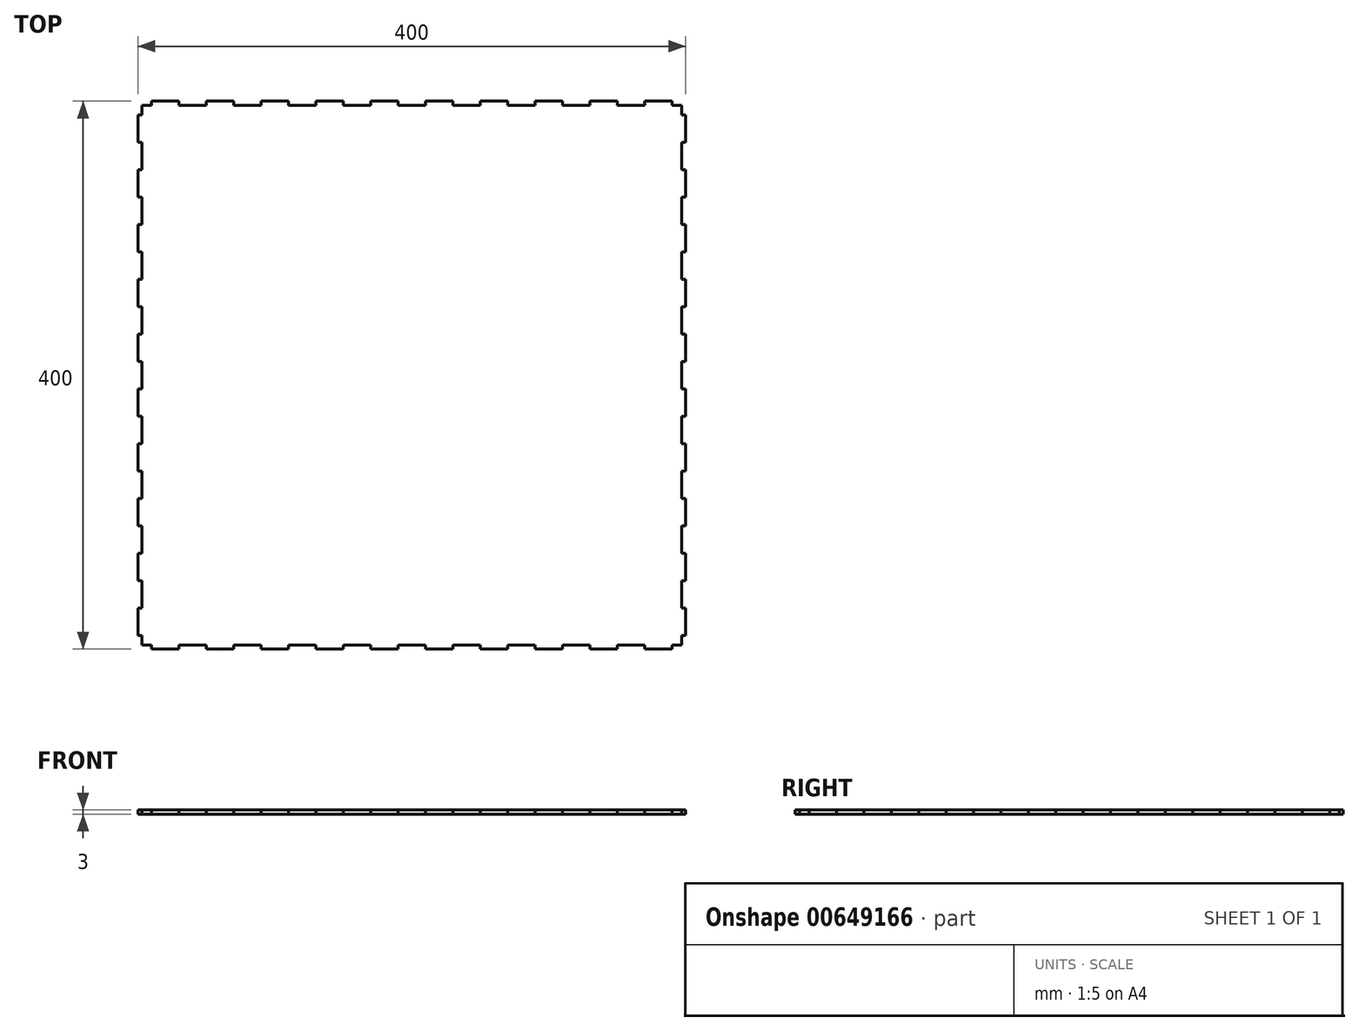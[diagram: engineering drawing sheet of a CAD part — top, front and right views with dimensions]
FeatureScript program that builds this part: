
annotation { "Feature Type Name" : "Feature", "Feature Type Description" : "" }
export const myFeature = defineFeature(function(context is Context, id is Id, definition is map)
    precondition{}
    {
        {
            var Q0;
            Q0=qCreatedBy(makeId("Top.planeOp"),FACE);
            var sketch = newSketch(context, id + "F0", { "sketchPlane" : qUnion([Q0])});
            skLineSegment(sketch, "E0.bottom", {"start": v(197, 197) * mm, "end": v(-197, 197) * mm});
            skLineSegment(sketch, "E0.top", {"start": v(197, -197) * mm, "end": v(-197, -197) * mm});
            skLineSegment(sketch, "E0.left", {"start": v(197, 197) * mm, "end": v(197, -197) * mm});
            skLineSegment(sketch, "E0.right", {"start": v(-197, 197) * mm, "end": v(-197, -197) * mm});
            skPoint(sketch, "E0.middle", {"position": v(0, 0) * mm});
            skSolve(sketch);
        }
        {
            var Q0;
            Q0 = qSketchRegion(id + "F0", true);
            extrude(context, id + "F1", {"entities" : qUnion([Q0]), "depth" : 3 * mm, "offsetDistance" : 25 * mm});
        }
        {
            var Q0;
            Q0=makeQuery(id+"F1.opExtrude","CAP_FACE",FACE,{"disambiguationData":[OSD([sQuery(id+"F0.wireOp",EDGE,"E0.bottom"),sQuery(id+"F0.wireOp",EDGE,"E0.top"),sQuery(id+"F0.wireOp",EDGE,"E0.left"),sQuery(id+"F0.wireOp",EDGE,"E0.right")])],"isStart":false});
            var sketch = newSketch(context, id + "F2", { "sketchPlane" : qUnion([Q0])});
            skLineSegment(sketch, "E1", {"start": v(-197, -197) * mm, "end": v(-190, -197) * mm, "construction": true});
            skLineSegment(sketch, "E2.bottom", {"start": v(-190, -197) * mm, "end": v(-170, -197) * mm});
            skLineSegment(sketch, "E2.top", {"start": v(-190, -200) * mm, "end": v(-170, -200) * mm});
            skLineSegment(sketch, "E2.left", {"start": v(-190, -197) * mm, "end": v(-190, -200) * mm});
            skLineSegment(sketch, "E2.right", {"start": v(-170, -197) * mm, "end": v(-170, -200) * mm});
            skLineSegment(sketch, "E3.1.0.0", {"start": v(-150, -197) * mm, "end": v(-130, -197) * mm});
            skLineSegment(sketch, "E3.1.0.1", {"start": v(-150, -197) * mm, "end": v(-150, -200) * mm});
            skLineSegment(sketch, "E3.1.0.2", {"start": v(-150, -200) * mm, "end": v(-130, -200) * mm});
            skLineSegment(sketch, "E3.1.0.3", {"start": v(-130, -197) * mm, "end": v(-130, -200) * mm});
            skLineSegment(sketch, "E3.2.0.0", {"start": v(-110, -197) * mm, "end": v(-90, -197) * mm});
            skLineSegment(sketch, "E3.2.0.1", {"start": v(-110, -197) * mm, "end": v(-110, -200) * mm});
            skLineSegment(sketch, "E3.2.0.2", {"start": v(-110, -200) * mm, "end": v(-90, -200) * mm});
            skLineSegment(sketch, "E3.2.0.3", {"start": v(-90, -197) * mm, "end": v(-90, -200) * mm});
            skLineSegment(sketch, "E3.direction1", {"start": v(-190, -197) * mm, "end": v(-150, -197) * mm, "construction": true});
            skLineSegment(sketch, "E4.0.3.0", {"start": v(-70, -197) * mm, "end": v(-50, -197) * mm});
            skLineSegment(sketch, "E4.3.3.0", {"start": v(-70, -197) * mm, "end": v(-70, -200) * mm});
            skLineSegment(sketch, "E4.6.3.0", {"start": v(-70, -200) * mm, "end": v(-50, -200) * mm});
            skLineSegment(sketch, "E4.9.3.0", {"start": v(-50, -197) * mm, "end": v(-50, -200) * mm});
            skLineSegment(sketch, "E4.0.4.0", {"start": v(-30, -197) * mm, "end": v(-10, -197) * mm});
            skLineSegment(sketch, "E4.3.4.0", {"start": v(-30, -197) * mm, "end": v(-30, -200) * mm});
            skLineSegment(sketch, "E4.6.4.0", {"start": v(-30, -200) * mm, "end": v(-10, -200) * mm});
            skLineSegment(sketch, "E4.9.4.0", {"start": v(-10, -197) * mm, "end": v(-10, -200) * mm});
            skLineSegment(sketch, "E4.0.5.0", {"start": v(10, -197) * mm, "end": v(30, -197) * mm});
            skLineSegment(sketch, "E4.3.5.0", {"start": v(10, -197) * mm, "end": v(10, -200) * mm});
            skLineSegment(sketch, "E4.6.5.0", {"start": v(10, -200) * mm, "end": v(30, -200) * mm});
            skLineSegment(sketch, "E4.9.5.0", {"start": v(30, -197) * mm, "end": v(30, -200) * mm});
            skLineSegment(sketch, "E4.0.6.0", {"start": v(50, -197) * mm, "end": v(70, -197) * mm});
            skLineSegment(sketch, "E4.3.6.0", {"start": v(50, -197) * mm, "end": v(50, -200) * mm});
            skLineSegment(sketch, "E4.6.6.0", {"start": v(50, -200) * mm, "end": v(70, -200) * mm});
            skLineSegment(sketch, "E4.9.6.0", {"start": v(70, -197) * mm, "end": v(70, -200) * mm});
            skLineSegment(sketch, "E4.0.7.0", {"start": v(90, -197) * mm, "end": v(110, -197) * mm});
            skLineSegment(sketch, "E4.3.7.0", {"start": v(90, -197) * mm, "end": v(90, -200) * mm});
            skLineSegment(sketch, "E4.6.7.0", {"start": v(90, -200) * mm, "end": v(110, -200) * mm});
            skLineSegment(sketch, "E4.9.7.0", {"start": v(110, -197) * mm, "end": v(110, -200) * mm});
            skLineSegment(sketch, "E4.0.8.0", {"start": v(130, -197) * mm, "end": v(150, -197) * mm});
            skLineSegment(sketch, "E4.3.8.0", {"start": v(130, -197) * mm, "end": v(130, -200) * mm});
            skLineSegment(sketch, "E4.6.8.0", {"start": v(130, -200) * mm, "end": v(150, -200) * mm});
            skLineSegment(sketch, "E4.9.8.0", {"start": v(150, -197) * mm, "end": v(150, -200) * mm});
            skLineSegment(sketch, "E5.0.9.0", {"start": v(170, -197) * mm, "end": v(190, -197) * mm});
            skLineSegment(sketch, "E5.3.9.0", {"start": v(170, -197) * mm, "end": v(170, -200) * mm});
            skLineSegment(sketch, "E5.6.9.0", {"start": v(170, -200) * mm, "end": v(190, -200) * mm});
            skLineSegment(sketch, "E5.9.9.0", {"start": v(190, -197) * mm, "end": v(190, -200) * mm});
            skLineSegment(sketch, "E6.1.0", {"start": v(197, 10) * mm, "end": v(197, 30) * mm});
            skLineSegment(sketch, "E6.1.1", {"start": v(197, 170) * mm, "end": v(197, 190) * mm});
            skLineSegment(sketch, "E6.1.2", {"start": v(200, -110) * mm, "end": v(200, -90) * mm});
            skLineSegment(sketch, "E6.1.3", {"start": v(197, -110) * mm, "end": v(197, -90) * mm});
            skLineSegment(sketch, "E6.1.4", {"start": v(200, -150) * mm, "end": v(200, -130) * mm});
            skLineSegment(sketch, "E6.1.5", {"start": v(197, 50) * mm, "end": v(197, 70) * mm});
            skLineSegment(sketch, "E6.1.6", {"start": v(197, -30) * mm, "end": v(197, -10) * mm});
            skLineSegment(sketch, "E6.1.7", {"start": v(197, 130) * mm, "end": v(197, 150) * mm});
            skLineSegment(sketch, "E6.1.8", {"start": v(197, -150) * mm, "end": v(197, -130) * mm});
            skLineSegment(sketch, "E6.1.9", {"start": v(197, -70) * mm, "end": v(197, -50) * mm});
            skLineSegment(sketch, "E6.1.10", {"start": v(197, -190) * mm, "end": v(197, -150) * mm, "construction": true});
            skLineSegment(sketch, "E6.1.11", {"start": v(197, 90) * mm, "end": v(197, 110) * mm});
            skLineSegment(sketch, "E6.1.12", {"start": v(200, 10) * mm, "end": v(200, 30) * mm});
            skLineSegment(sketch, "E6.1.13", {"start": v(200, 170) * mm, "end": v(200, 190) * mm});
            skLineSegment(sketch, "E6.1.14", {"start": v(200, 50) * mm, "end": v(200, 70) * mm});
            skLineSegment(sketch, "E6.1.15", {"start": v(200, -70) * mm, "end": v(200, -50) * mm});
            skLineSegment(sketch, "E6.1.16", {"start": v(200, 90) * mm, "end": v(200, 110) * mm});
            skLineSegment(sketch, "E6.1.17", {"start": v(200, -30) * mm, "end": v(200, -10) * mm});
            skLineSegment(sketch, "E6.1.18", {"start": v(200, 130) * mm, "end": v(200, 150) * mm});
            skLineSegment(sketch, "E6.1.19", {"start": v(200, -190) * mm, "end": v(200, -170) * mm});
            skLineSegment(sketch, "E6.1.20", {"start": v(197, -190) * mm, "end": v(197, -170) * mm});
            skLineSegment(sketch, "E6.1.21", {"start": v(197, -90) * mm, "end": v(200, -90) * mm});
            skLineSegment(sketch, "E6.1.22", {"start": v(197, 30) * mm, "end": v(200, 30) * mm});
            skLineSegment(sketch, "E6.1.23", {"start": v(197, 190) * mm, "end": v(200, 190) * mm});
            skLineSegment(sketch, "E6.1.24", {"start": v(197, -110) * mm, "end": v(200, -110) * mm});
            skLineSegment(sketch, "E6.1.25", {"start": v(197, 130) * mm, "end": v(200, 130) * mm});
            skLineSegment(sketch, "E6.1.26", {"start": v(197, -30) * mm, "end": v(200, -30) * mm});
            skLineSegment(sketch, "E6.1.27", {"start": v(197, 170) * mm, "end": v(200, 170) * mm});
            skLineSegment(sketch, "E6.1.28", {"start": v(197, 90) * mm, "end": v(200, 90) * mm});
            skLineSegment(sketch, "E6.1.29", {"start": v(197, -170) * mm, "end": v(200, -170) * mm});
            skLineSegment(sketch, "E6.1.30", {"start": v(197, -70) * mm, "end": v(200, -70) * mm});
            skLineSegment(sketch, "E6.1.31", {"start": v(197, -50) * mm, "end": v(200, -50) * mm});
            skLineSegment(sketch, "E6.1.32", {"start": v(197, 110) * mm, "end": v(200, 110) * mm});
            skLineSegment(sketch, "E6.1.33", {"start": v(197, -10) * mm, "end": v(200, -10) * mm});
            skLineSegment(sketch, "E6.1.34", {"start": v(197, 150) * mm, "end": v(200, 150) * mm});
            skLineSegment(sketch, "E6.1.35", {"start": v(197, 50) * mm, "end": v(200, 50) * mm});
            skLineSegment(sketch, "E6.1.36", {"start": v(197, 70) * mm, "end": v(200, 70) * mm});
            skLineSegment(sketch, "E6.1.37", {"start": v(197, 10) * mm, "end": v(200, 10) * mm});
            skLineSegment(sketch, "E6.1.38", {"start": v(197, -130) * mm, "end": v(200, -130) * mm});
            skLineSegment(sketch, "E6.1.39", {"start": v(197, -150) * mm, "end": v(200, -150) * mm});
            skLineSegment(sketch, "E6.1.40", {"start": v(197, -190) * mm, "end": v(200, -190) * mm});
            skLineSegment(sketch, "E6.1.41", {"start": v(197, -197) * mm, "end": v(197, -190) * mm, "construction": true});
            skLineSegment(sketch, "E6.2.0", {"start": v(-10, 197) * mm, "end": v(-30, 197) * mm});
            skLineSegment(sketch, "E6.2.1", {"start": v(-170, 197) * mm, "end": v(-190, 197) * mm});
            skLineSegment(sketch, "E6.2.2", {"start": v(110, 200) * mm, "end": v(90, 200) * mm});
            skLineSegment(sketch, "E6.2.3", {"start": v(110, 197) * mm, "end": v(90, 197) * mm});
            skLineSegment(sketch, "E6.2.4", {"start": v(150, 200) * mm, "end": v(130, 200) * mm});
            skLineSegment(sketch, "E6.2.5", {"start": v(-50, 197) * mm, "end": v(-70, 197) * mm});
            skLineSegment(sketch, "E6.2.6", {"start": v(30, 197) * mm, "end": v(10, 197) * mm});
            skLineSegment(sketch, "E6.2.7", {"start": v(-130, 197) * mm, "end": v(-150, 197) * mm});
            skLineSegment(sketch, "E6.2.8", {"start": v(150, 197) * mm, "end": v(130, 197) * mm});
            skLineSegment(sketch, "E6.2.9", {"start": v(70, 197) * mm, "end": v(50, 197) * mm});
            skLineSegment(sketch, "E6.2.10", {"start": v(190, 197) * mm, "end": v(150, 197) * mm, "construction": true});
            skLineSegment(sketch, "E6.2.11", {"start": v(-90, 197) * mm, "end": v(-110, 197) * mm});
            skLineSegment(sketch, "E6.2.12", {"start": v(-10, 200) * mm, "end": v(-30, 200) * mm});
            skLineSegment(sketch, "E6.2.13", {"start": v(-170, 200) * mm, "end": v(-190, 200) * mm});
            skLineSegment(sketch, "E6.2.14", {"start": v(-50, 200) * mm, "end": v(-70, 200) * mm});
            skLineSegment(sketch, "E6.2.15", {"start": v(70, 200) * mm, "end": v(50, 200) * mm});
            skLineSegment(sketch, "E6.2.16", {"start": v(-90, 200) * mm, "end": v(-110, 200) * mm});
            skLineSegment(sketch, "E6.2.17", {"start": v(30, 200) * mm, "end": v(10, 200) * mm});
            skLineSegment(sketch, "E6.2.18", {"start": v(-130, 200) * mm, "end": v(-150, 200) * mm});
            skLineSegment(sketch, "E6.2.19", {"start": v(190, 200) * mm, "end": v(170, 200) * mm});
            skLineSegment(sketch, "E6.2.20", {"start": v(190, 197) * mm, "end": v(170, 197) * mm});
            skLineSegment(sketch, "E6.2.21", {"start": v(90, 197) * mm, "end": v(90, 200) * mm});
            skLineSegment(sketch, "E6.2.22", {"start": v(-30, 197) * mm, "end": v(-30, 200) * mm});
            skLineSegment(sketch, "E6.2.23", {"start": v(-190, 197) * mm, "end": v(-190, 200) * mm});
            skLineSegment(sketch, "E6.2.24", {"start": v(110, 197) * mm, "end": v(110, 200) * mm});
            skLineSegment(sketch, "E6.2.25", {"start": v(-130, 197) * mm, "end": v(-130, 200) * mm});
            skLineSegment(sketch, "E6.2.26", {"start": v(30, 197) * mm, "end": v(30, 200) * mm});
            skLineSegment(sketch, "E6.2.27", {"start": v(-170, 197) * mm, "end": v(-170, 200) * mm});
            skLineSegment(sketch, "E6.2.28", {"start": v(-90, 197) * mm, "end": v(-90, 200) * mm});
            skLineSegment(sketch, "E6.2.29", {"start": v(170, 197) * mm, "end": v(170, 200) * mm});
            skLineSegment(sketch, "E6.2.30", {"start": v(70, 197) * mm, "end": v(70, 200) * mm});
            skLineSegment(sketch, "E6.2.31", {"start": v(50, 197) * mm, "end": v(50, 200) * mm});
            skLineSegment(sketch, "E6.2.32", {"start": v(-110, 197) * mm, "end": v(-110, 200) * mm});
            skLineSegment(sketch, "E6.2.33", {"start": v(10, 197) * mm, "end": v(10, 200) * mm});
            skLineSegment(sketch, "E6.2.34", {"start": v(-150, 197) * mm, "end": v(-150, 200) * mm});
            skLineSegment(sketch, "E6.2.35", {"start": v(-50, 197) * mm, "end": v(-50, 200) * mm});
            skLineSegment(sketch, "E6.2.36", {"start": v(-70, 197) * mm, "end": v(-70, 200) * mm});
            skLineSegment(sketch, "E6.2.37", {"start": v(-10, 197) * mm, "end": v(-10, 200) * mm});
            skLineSegment(sketch, "E6.2.38", {"start": v(130, 197) * mm, "end": v(130, 200) * mm});
            skLineSegment(sketch, "E6.2.39", {"start": v(150, 197) * mm, "end": v(150, 200) * mm});
            skLineSegment(sketch, "E6.2.40", {"start": v(190, 197) * mm, "end": v(190, 200) * mm});
            skLineSegment(sketch, "E6.2.41", {"start": v(197, 197) * mm, "end": v(190, 197) * mm, "construction": true});
            skLineSegment(sketch, "E6.3.0", {"start": v(-197, -10) * mm, "end": v(-197, -30) * mm});
            skLineSegment(sketch, "E6.3.1", {"start": v(-197, -170) * mm, "end": v(-197, -190) * mm});
            skLineSegment(sketch, "E6.3.2", {"start": v(-200, 110) * mm, "end": v(-200, 90) * mm});
            skLineSegment(sketch, "E6.3.3", {"start": v(-197, 110) * mm, "end": v(-197, 90) * mm});
            skLineSegment(sketch, "E6.3.4", {"start": v(-200, 150) * mm, "end": v(-200, 130) * mm});
            skLineSegment(sketch, "E6.3.5", {"start": v(-197, -50) * mm, "end": v(-197, -70) * mm});
            skLineSegment(sketch, "E6.3.6", {"start": v(-197, 30) * mm, "end": v(-197, 10) * mm});
            skLineSegment(sketch, "E6.3.7", {"start": v(-197, -130) * mm, "end": v(-197, -150) * mm});
            skLineSegment(sketch, "E6.3.8", {"start": v(-197, 150) * mm, "end": v(-197, 130) * mm});
            skLineSegment(sketch, "E6.3.9", {"start": v(-197, 70) * mm, "end": v(-197, 50) * mm});
            skLineSegment(sketch, "E6.3.10", {"start": v(-197, 190) * mm, "end": v(-197, 150) * mm, "construction": true});
            skLineSegment(sketch, "E6.3.11", {"start": v(-197, -90) * mm, "end": v(-197, -110) * mm});
            skLineSegment(sketch, "E6.3.12", {"start": v(-200, -10) * mm, "end": v(-200, -30) * mm});
            skLineSegment(sketch, "E6.3.13", {"start": v(-200, -170) * mm, "end": v(-200, -190) * mm});
            skLineSegment(sketch, "E6.3.14", {"start": v(-200, -50) * mm, "end": v(-200, -70) * mm});
            skLineSegment(sketch, "E6.3.15", {"start": v(-200, 70) * mm, "end": v(-200, 50) * mm});
            skLineSegment(sketch, "E6.3.16", {"start": v(-200, -90) * mm, "end": v(-200, -110) * mm});
            skLineSegment(sketch, "E6.3.17", {"start": v(-200, 30) * mm, "end": v(-200, 10) * mm});
            skLineSegment(sketch, "E6.3.18", {"start": v(-200, -130) * mm, "end": v(-200, -150) * mm});
            skLineSegment(sketch, "E6.3.19", {"start": v(-200, 190) * mm, "end": v(-200, 170) * mm});
            skLineSegment(sketch, "E6.3.20", {"start": v(-197, 190) * mm, "end": v(-197, 170) * mm});
            skLineSegment(sketch, "E6.3.21", {"start": v(-197, 90) * mm, "end": v(-200, 90) * mm});
            skLineSegment(sketch, "E6.3.22", {"start": v(-197, -30) * mm, "end": v(-200, -30) * mm});
            skLineSegment(sketch, "E6.3.23", {"start": v(-197, -190) * mm, "end": v(-200, -190) * mm});
            skLineSegment(sketch, "E6.3.24", {"start": v(-197, 110) * mm, "end": v(-200, 110) * mm});
            skLineSegment(sketch, "E6.3.25", {"start": v(-197, -130) * mm, "end": v(-200, -130) * mm});
            skLineSegment(sketch, "E6.3.26", {"start": v(-197, 30) * mm, "end": v(-200, 30) * mm});
            skLineSegment(sketch, "E6.3.27", {"start": v(-197, -170) * mm, "end": v(-200, -170) * mm});
            skLineSegment(sketch, "E6.3.28", {"start": v(-197, -90) * mm, "end": v(-200, -90) * mm});
            skLineSegment(sketch, "E6.3.29", {"start": v(-197, 170) * mm, "end": v(-200, 170) * mm});
            skLineSegment(sketch, "E6.3.30", {"start": v(-197, 70) * mm, "end": v(-200, 70) * mm});
            skLineSegment(sketch, "E6.3.31", {"start": v(-197, 50) * mm, "end": v(-200, 50) * mm});
            skLineSegment(sketch, "E6.3.32", {"start": v(-197, -110) * mm, "end": v(-200, -110) * mm});
            skLineSegment(sketch, "E6.3.33", {"start": v(-197, 10) * mm, "end": v(-200, 10) * mm});
            skLineSegment(sketch, "E6.3.34", {"start": v(-197, -150) * mm, "end": v(-200, -150) * mm});
            skLineSegment(sketch, "E6.3.35", {"start": v(-197, -50) * mm, "end": v(-200, -50) * mm});
            skLineSegment(sketch, "E6.3.36", {"start": v(-197, -70) * mm, "end": v(-200, -70) * mm});
            skLineSegment(sketch, "E6.3.37", {"start": v(-197, -10) * mm, "end": v(-200, -10) * mm});
            skLineSegment(sketch, "E6.3.38", {"start": v(-197, 130) * mm, "end": v(-200, 130) * mm});
            skLineSegment(sketch, "E6.3.39", {"start": v(-197, 150) * mm, "end": v(-200, 150) * mm});
            skLineSegment(sketch, "E6.3.40", {"start": v(-197, 190) * mm, "end": v(-200, 190) * mm});
            skLineSegment(sketch, "E6.3.41", {"start": v(-197, 197) * mm, "end": v(-197, 190) * mm, "construction": true});
            skPoint(sketch, "E6.center", {"position": v(0, 0) * mm});
            skSolve(sketch);
        }
        {
            var Q0;
            Q0 = qSketchRegion(id + "F2", true);
            var Q1;
            Q1=makeQuery(id+"F1.opExtrude","CAP_FACE",FACE,{"disambiguationData":[OSD([sQuery(id+"F0.wireOp",EDGE,"E0.bottom"),sQuery(id+"F0.wireOp",EDGE,"E0.top"),sQuery(id+"F0.wireOp",EDGE,"E0.left"),sQuery(id+"F0.wireOp",EDGE,"E0.right")])],"isStart":true});
            extrude(context, id + "F3", {"entities" : qUnion([Q0]), "operationType" : NewBodyOperationType.ADD, "endBound" : BoundingType.UP_TO_SURFACE, "oppositeDirection" : true, "depth" : 25 * mm, "endBoundEntityFace" : qUnion([Q1]), "offsetDistance" : 25 * mm});
        }
    });
